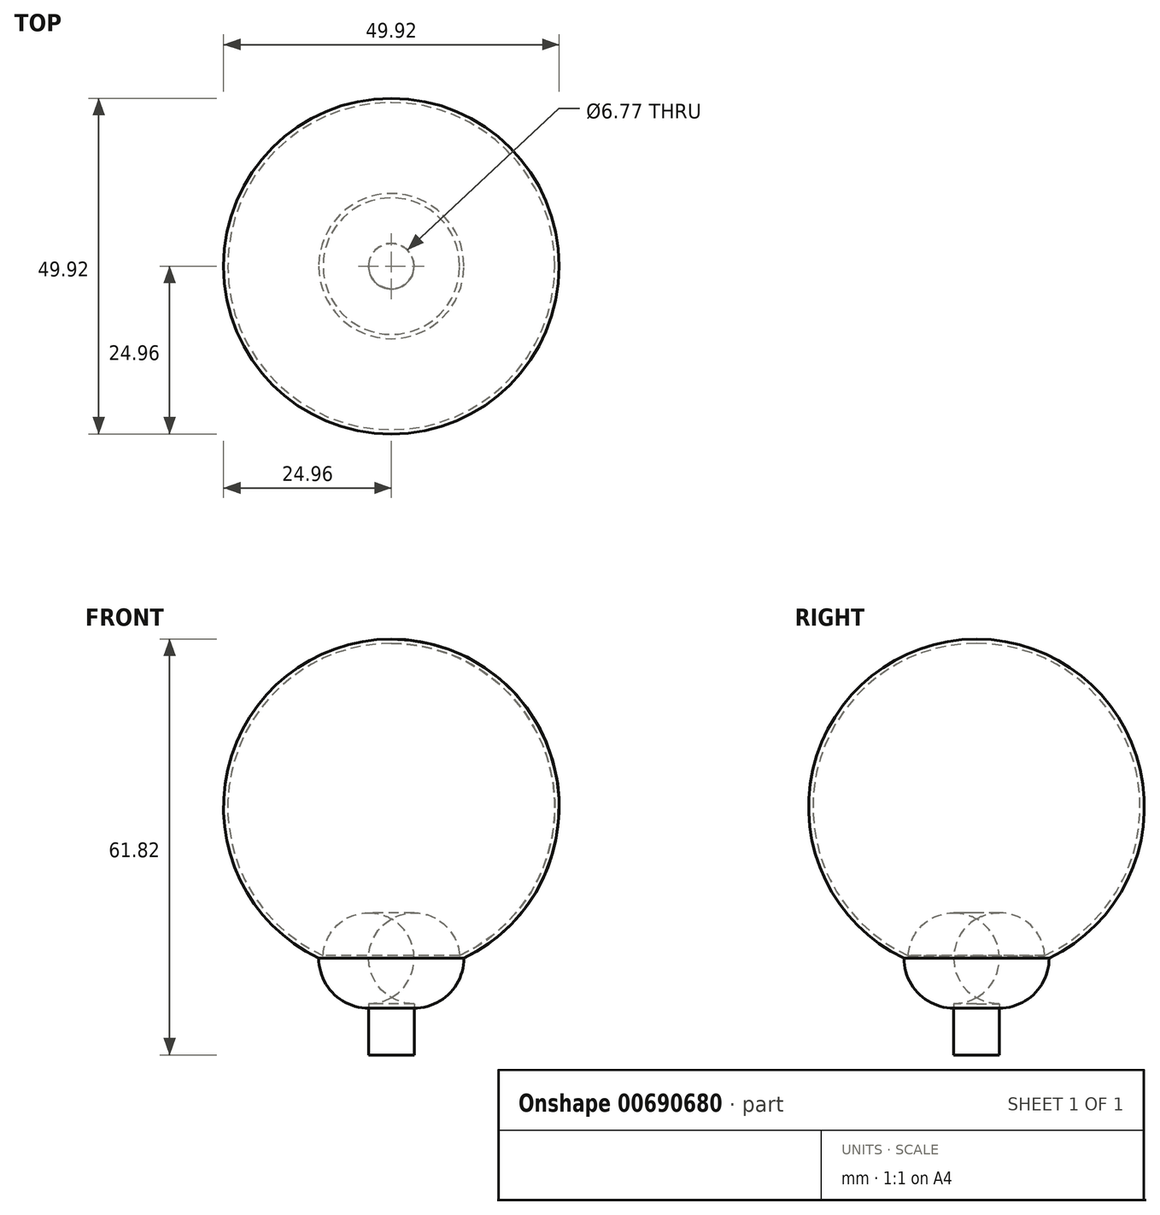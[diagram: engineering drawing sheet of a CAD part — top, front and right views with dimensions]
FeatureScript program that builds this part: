
annotation { "Feature Type Name" : "Feature", "Feature Type Description" : "" }
export const myFeature = defineFeature(function(context is Context, id is Id, definition is map)
    precondition{}
    {
        {
            var Q0;
            Q0=qCreatedBy(makeId("Front.planeOp"),FACE);
            var sketch = newSketch(context, id + "F0", { "sketchPlane" : qUnion([Q0])});
            skLineSegment(sketch, "E0", {"start": v(0, 0) * mm, "end": v(3.39, 0) * mm});
            skArc(sketch, "E1", {"start": v(3.39, 0) * mm, "mid": v(8.63, 2.17) * mm, "end": v(10.8, 7.4) * mm});
            skLineSegment(sketch, "E2", {"start": v(0, 0) * mm, "end": v(0, 54.86) * mm});
            skLineSegment(sketch, "E3", {"start": v(-3.79, 54.86) * mm, "end": v(-3.79, 7.4) * mm, "construction": true});
            skLineSegment(sketch, "E4", {"start": v(-3.79, 31.14) * mm, "end": v(4.98, 31.14) * mm, "construction": true});
            skLineSegment(sketch, "E5", {"start": v(3.39, 7.4) * mm, "end": v(0, 7.4) * mm, "construction": true});
            skLineSegment(sketch, "E6", {"start": v(0, 7.4) * mm, "end": v(14.9, 7.4) * mm, "construction": true});
            skArc(sketch, "E7", {"start": v(10.8, 7.4) * mm, "mid": v(24.33, 35.44) * mm, "end": v(0, 54.86) * mm});
            skLineSegment(sketch, "E8.top", {"start": v(0, -6.96) * mm, "end": v(3.39, -6.96) * mm});
            skLineSegment(sketch, "E8.left", {"start": v(0, 0) * mm, "end": v(0, -6.96) * mm});
            skLineSegment(sketch, "E8.right", {"start": v(3.39, 0) * mm, "end": v(3.39, -6.96) * mm});
            skSolve(sketch);
        }
        {
            var Q0;
            Q0=makeQuery(id+"F0.imprint","IMPRINT",FACE,{"disambiguationData":[TD([[makeQuery(id+"F0.imprint","IMPRINT",EDGE,{"derivedFrom":sQuery(id+"F0.wireOp",EDGE,"E1")}),1.0]])]});
            var Q1;
            Q1=sQuery(id+"F0.wireOp",EDGE,"E2");
            revolve(context, id + "F1", {"surfaceOperationType" : NewSurfaceOperationType.NEW, "entities" : qUnion([Q0]), "axis" : qUnion([Q1]), "revolveType" : RevolveType.FULL});
        }
        {
            var Q0;
            Q0=makeQuery(id+"F1.opRevolve","SWEPT_FACE",FACE,{"disambiguationData":[OSD([sQuery(id+"F0.wireOp",EDGE,"E0")])]});
            var Q1;
            Q1=makeQuery(id+"F1.opRevolve","SWEPT_FACE",FACE,{"disambiguationData":[OSD([sQuery(id+"F0.wireOp",EDGE,"E0")])]});
            shell(context, id + "F2", {"entities" : qUnion([Q0, Q1]), "thickness" : 0.64 * mm});
        }
        {
            var Q0;
            Q0=makeQuery(id+"F0.imprint","IMPRINT",FACE,{"disambiguationData":[TD([[makeQuery(id+"F0.imprint","IMPRINT",EDGE,{"derivedFrom":sQuery(id+"F0.wireOp",EDGE,"E0")}),-1.0]])]});
            var Q1;
            Q1=sQuery(id+"F0.wireOp",EDGE,"E2");
            revolve(context, id + "F3", {"surfaceOperationType" : NewSurfaceOperationType.NEW, "entities" : qUnion([Q0]), "axis" : qUnion([Q1]), "revolveType" : RevolveType.FULL});
        }
    });
